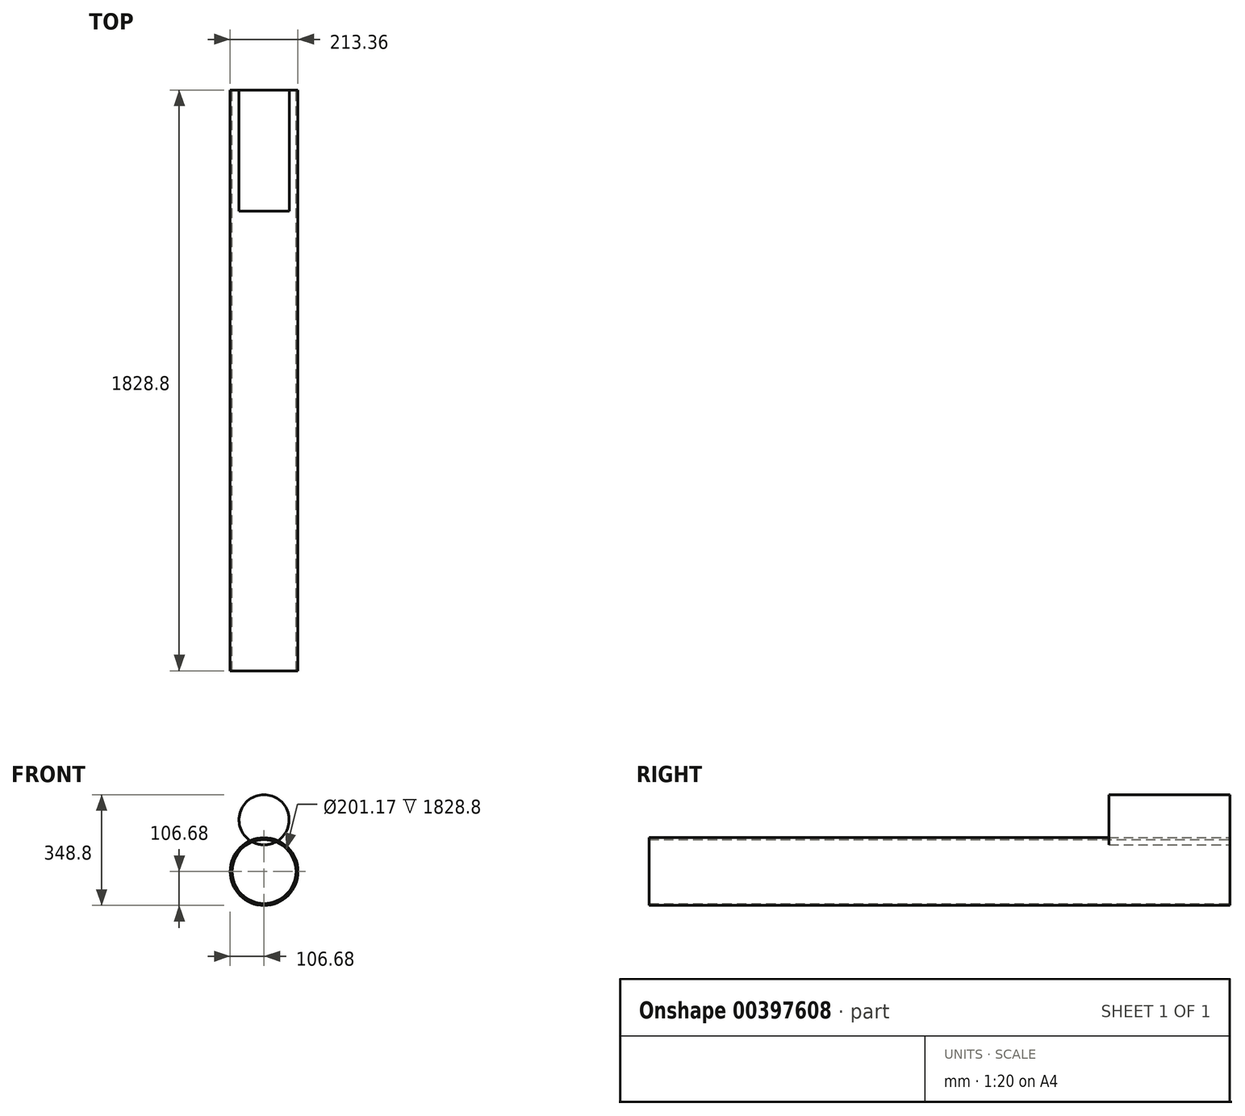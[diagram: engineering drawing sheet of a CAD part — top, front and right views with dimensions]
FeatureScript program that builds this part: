
annotation { "Feature Type Name" : "Feature", "Feature Type Description" : "" }
export const myFeature = defineFeature(function(context is Context, id is Id, definition is map)
    precondition{}
    {
        {
            var Q0;
            Q0=qCreatedBy(makeId("Front.planeOp"),FACE);
            var sketch = newSketch(context, id + "F0", { "sketchPlane" : qUnion([Q0])});
            skCircle(sketch, "E0", {"center": v(0, 0) * mm, "radius": 106.68 * mm});
            skCircle(sketch, "E1", {"center": v(0, 0) * mm, "radius": 100.58 * mm});
            skSolve(sketch);
        }
        {
            var Q0;
            Q0=makeQuery(id+"F0.imprint","IMPRINT",FACE,{"disambiguationData":[TD([[makeQuery(id+"F0.imprint","IMPRINT",EDGE,{"derivedFrom":sQuery(id+"F0.wireOp",EDGE,"E0")}),1.0]])]});
            extrude(context, id + "F1", {"entities" : qUnion([Q0]), "depth" : 1828.8 * mm});
        }
        {
            var Q0;
            Q0=qCreatedBy(makeId("Front.planeOp"),FACE);
            var sketch = newSketch(context, id + "F2", { "sketchPlane" : qUnion([Q0])});
            skCircle(sketch, "E2", {"center": v(0, 163.2) * mm, "radius": 75.12 * mm});
            skCircle(sketch, "E3", {"center": v(0, 163.2) * mm, "radius": 78.93 * mm});
            skSolve(sketch);
        }
        {
            var Q0;
            Q0=makeQuery(id+"F2.imprint","IMPRINT",FACE,{"disambiguationData":[TD([[makeQuery(id+"F2.imprint","IMPRINT",EDGE,{"derivedFrom":sQuery(id+"F2.wireOp",EDGE,"E2")}),-1.0]])]});
            var Q1;
            Q1=makeQuery(id+"F2.imprint","IMPRINT",FACE,{"disambiguationData":[TD([[makeQuery(id+"F2.imprint","IMPRINT",EDGE,{"derivedFrom":sQuery(id+"F2.wireOp",EDGE,"E2")}),1.0]])]});
            extrude(context, id + "F3", {"entities" : qUnion([Q0, Q1]), "depth" : 381 * mm});
        }
    });
